# Revit family: Sink-Pedestal-Lavatory-KOHLER-Brive-K-8703IN_1
name_source: partatom
category: Plumbing Fixtures
revit_build: Autodesk Revit 2017 (Build: 20160225_1515(x64)
units: mm (PartAtom-declared; Revit-internal decimal feet)

## family parameters
Cut with Voids When Loaded = No
Host = Face
OmniClass Number = 23.31.13.00
OmniClass Title = Sinks
Part Type = Normal
Room Calculation Point = No
Round Connector Dimension = Use Diameter
Shared = No

## types (3) — shared parameters
ADA Compliant = No
Assembly Code = D2010400
CW Connection = No
Cold Water Inlet = Cold Water Inlet
Date Modified = 08/27/2020
Default Elevation = 36"
Description = Wall Mount Lavatory With Single Faucet Hole
Drain Included = No
HW Connection = No
Height = 9 1/4"
Hot Water Inlet = Hot Water Inlet
Length = 18 1/4"
Manufacturer = KOHLER Co.
Master Format 2014 = 22 41 16
Master Format 2014 Name = Residential Lavatories and Sinks
Material = Vitreous China
Product Name = Brive
URL = https://www.kohler.co.in
Vent Connection = No
Waste Connection = Yes
Waste Water Outlet = Waste Water Outlet
WaterSense Certified = No
Width = 21 1/4"

## per-type parameters (varying)
| type | Finish | Model | Product Page URL | Type |
| 0-White | Kohler-Vitreous_China-0-White | K-8703IN-1WH-0 | https://www.kohler.co.in | 1 |
| 96-Biscuit | Kohler-Vitreous_China-96-Biscuit | K-8703IN-1WH-96 |  | 2 |
| 1WHZ, 96-Biscuit | Kohler-Vitreous_China-96-Biscuit | K-8703IN-1WHZ-96 |  | 3 |

## geometry (parser evidence)
native form markers: Sweep x6
no freeform markers — native parametric forms only
